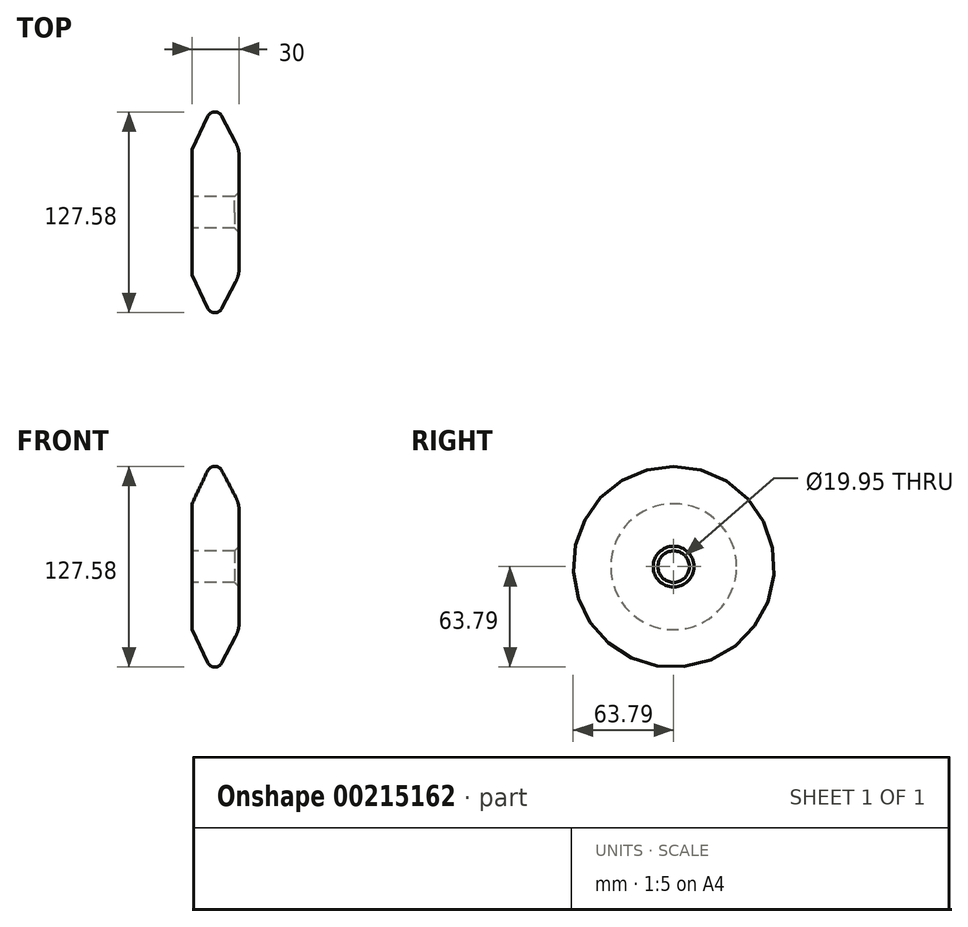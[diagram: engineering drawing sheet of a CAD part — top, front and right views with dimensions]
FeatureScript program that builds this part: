
annotation { "Feature Type Name" : "Feature", "Feature Type Description" : "" }
export const myFeature = defineFeature(function(context is Context, id is Id, definition is map)
    precondition{}
    {
        {
            var Q0;
            Q0=qCreatedBy(makeId("Front.planeOp"),FACE);
            var sketch = newSketch(context, id + "F3", { "sketchPlane" : qUnion([Q0])});
            skLineSegment(sketch, "E0", {"start": v(-106.64, 0) * mm, "end": v(124.24, 0) * mm});
            skSolve(sketch);
        }
        {
            var Q0;
            Q0=qCreatedBy(makeId("Front.planeOp"),FACE);
            var sketch = newSketch(context, id + "F4", { "sketchPlane" : qUnion([Q0])});
            skCircle(sketch, "E1", {"center": v(60.45, 50.35) * mm, "radius": 29.07 * mm});
            skSolve(sketch);
        }
        {
            var Q0;
            Q0=sQuery(id+"F4.wireOp",EDGE,"E1");
            var Q1;
            Q1=sQuery(id+"F3.wireOp",EDGE,"E0");
            revolve(context, id + "F5", {"bodyType" : ToolBodyType.SURFACE, "surfaceEntities" : qUnion([Q0]), "axis" : qUnion([Q1]), "revolveType" : RevolveType.FULL});
        }
        {
            var Q0;
            Q0=qCreatedBy(makeId("Front.planeOp"),FACE);
            var sketch = newSketch(context, id + "F0", { "sketchPlane" : qUnion([Q0])});
            skLineSegment(sketch, "E2.bottom", {"start": v(-48.7, 39.97) * mm, "end": v(-18.7, 39.97) * mm});
            skLineSegment(sketch, "E2.top", {"start": v(-48.7, 9.97) * mm, "end": v(-18.7, 9.97) * mm});
            skLineSegment(sketch, "E2.left", {"start": v(-48.7, 39.97) * mm, "end": v(-48.7, 9.97) * mm});
            skLineSegment(sketch, "E2.right", {"start": v(-18.7, 39.97) * mm, "end": v(-18.7, 9.97) * mm});
            skLineSegment(sketch, "E3", {"start": v(-18.7, 39.97) * mm, "end": v(-34.55, 69.97) * mm});
            skLineSegment(sketch, "E4", {"start": v(-34.55, 69.97) * mm, "end": v(-48.7, 39.97) * mm});
            skSolve(sketch);
        }
        {
            var Q0;
            Q0 = qSketchRegion(id + "F0", true);
            var Q1;
            Q1=sQuery(id+"F3.wireOp",EDGE,"E0");
            revolve(context, id + "F6", {"entities" : qUnion([Q0]), "axis" : qUnion([Q1]), "revolveType" : RevolveType.FULL});
        }
        {
            var Q0;
            Q0=makeQuery(id+"F6.opRevolve","SWEPT_EDGE",EDGE,{"disambiguationData":[OSD([sQuery(id+"F0.wireOp",EDGE,"E3"),sQuery(id+"F0.wireOp",EDGE,"E4")])]});
            fillet(context, id + "F7", {"entities" : qUnion([Q0]), "radius" : 5 * mm, "tangentPropagation" : true, "allowEdgeOverflow" : false});
        }
        {
            var Q0;
            Q0=makeQuery(id+"F6.opRevolve","SWEPT_EDGE",EDGE,{"disambiguationData":[OSD([sQuery(id+"F0.wireOp",EDGE,"E2.bottom"),sQuery(id+"F0.wireOp",EDGE,"E2.right"),sQuery(id+"F0.wireOp",EDGE,"E3")])]});
            fillet(context, id + "F1", {"entities" : qUnion([Q0]), "radius" : 20 * mm, "tangentPropagation" : true, "allowEdgeOverflow" : false});
        }
        {
            var Q0;
            Q0=makeQuery(id+"F6.opRevolve","SWEPT_EDGE",EDGE,{"disambiguationData":[OSD([sQuery(id+"F0.wireOp",EDGE,"E2.top"),sQuery(id+"F0.wireOp",EDGE,"E2.right")])]});
            chamfer(context, id + "F2", {"entities" : qUnion([Q0]), "width" : 3 * mm, "tangentPropagation" : true});
        }
    });
